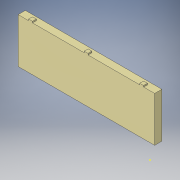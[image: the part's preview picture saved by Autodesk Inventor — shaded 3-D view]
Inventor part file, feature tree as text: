
AUTODESK INVENTOR PART (.ipt)
format: ipt  version: 2016 (Build 200138000, 138)  size: 126,976 bytes
history: native  units: in
note: dims shown in document units (in); Inventor stores cm internally (conversion verified against a paired STEP export)
features: sketch x3, extrude x2
ambient origin geometry x8: Origin, YZ Plane, XZ Plane, XY Plane, X Axis, Y Axis, Z Axis, Center Point
bodies: Solid1 (feature_tree)
feature tree (5):
  extrude  "Extrusion1"  Depth=2.14in
  extrude  "Extrusion2"  Depth=0.185in
  sketch  "Sketch3"  dims[d5=0.185in d6=0.5in d7=1.1811in d9=2.645in d10=0.3937in d12=1.0in d14=0.065in d15=0.0in]
  sketch  "Sketch1"  dims[d0=6.5in d1=2.14in]
  sketch  "Sketch2"  dims[d2=0.345in d3=0.0in d4=0.185in]
